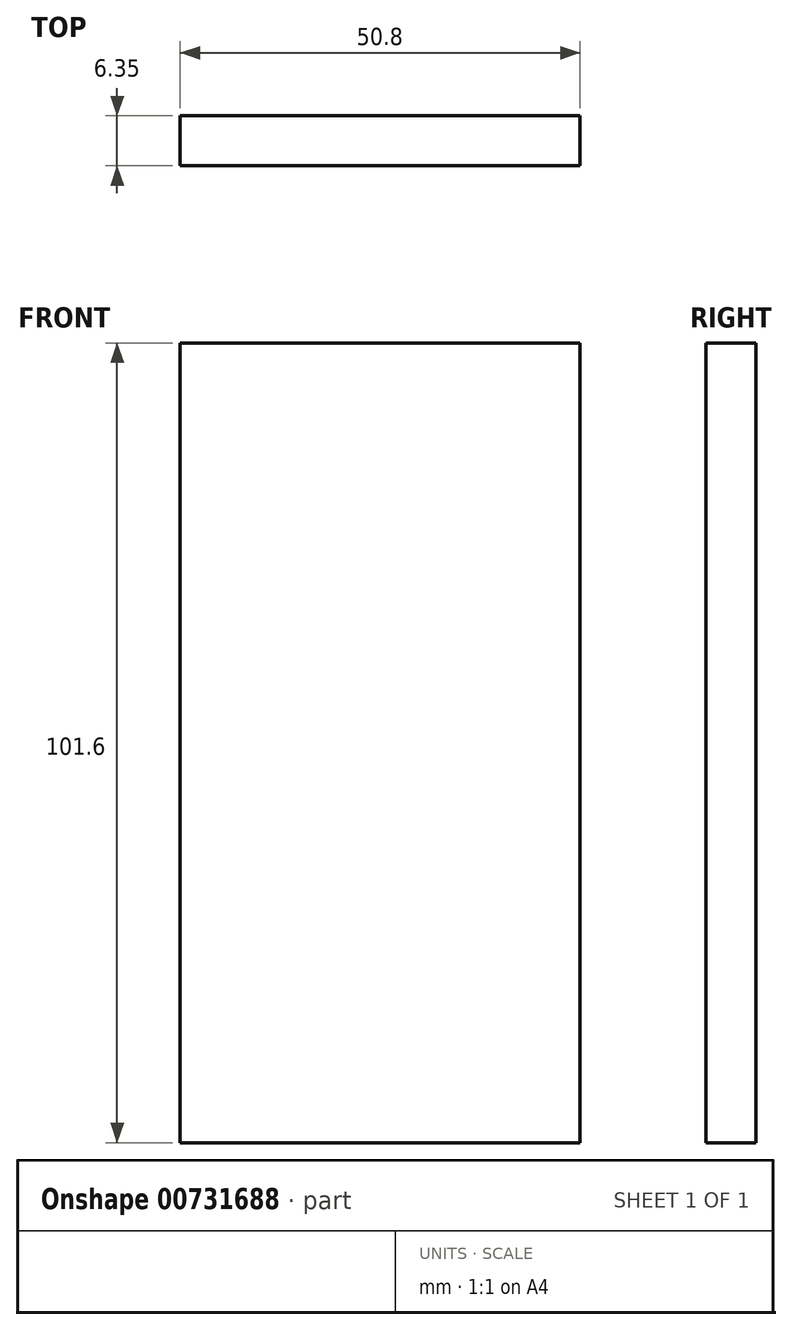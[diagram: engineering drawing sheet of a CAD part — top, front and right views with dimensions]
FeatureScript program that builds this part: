
annotation { "Feature Type Name" : "Feature", "Feature Type Description" : "" }
export const myFeature = defineFeature(function(context is Context, id is Id, definition is map)
    precondition{}
    {
        {
            var Q0;
            Q0=qCreatedBy(makeId("Front.planeOp"),FACE);
            var sketch = newSketch(context, id + "F0", { "sketchPlane" : qUnion([Q0])});
            skLineSegment(sketch, "E0.bottom", {"start": v(-32.2, 32.13) * mm, "end": v(18.6, 32.13) * mm});
            skLineSegment(sketch, "E0.top", {"start": v(-32.2, -69.47) * mm, "end": v(18.6, -69.47) * mm});
            skLineSegment(sketch, "E0.left", {"start": v(-32.2, 32.13) * mm, "end": v(-32.2, -69.47) * mm});
            skLineSegment(sketch, "E0.right", {"start": v(18.6, 32.13) * mm, "end": v(18.6, -69.47) * mm});
            skSolve(sketch);
        }
        {
            var Q0;
            Q0=makeQuery(id+"F0.imprint","IMPRINT",FACE,{"disambiguationData":[TD([[makeQuery(id+"F0.imprint","IMPRINT",EDGE,{"derivedFrom":sQuery(id+"F0.wireOp",EDGE,"E0.bottom")}),-1.0]])]});
            extrude(context, id + "F1", {"entities" : qUnion([Q0]), "depth" : 6.35 * mm, "offsetDistance" : 25.4 * mm});
        }
    });
